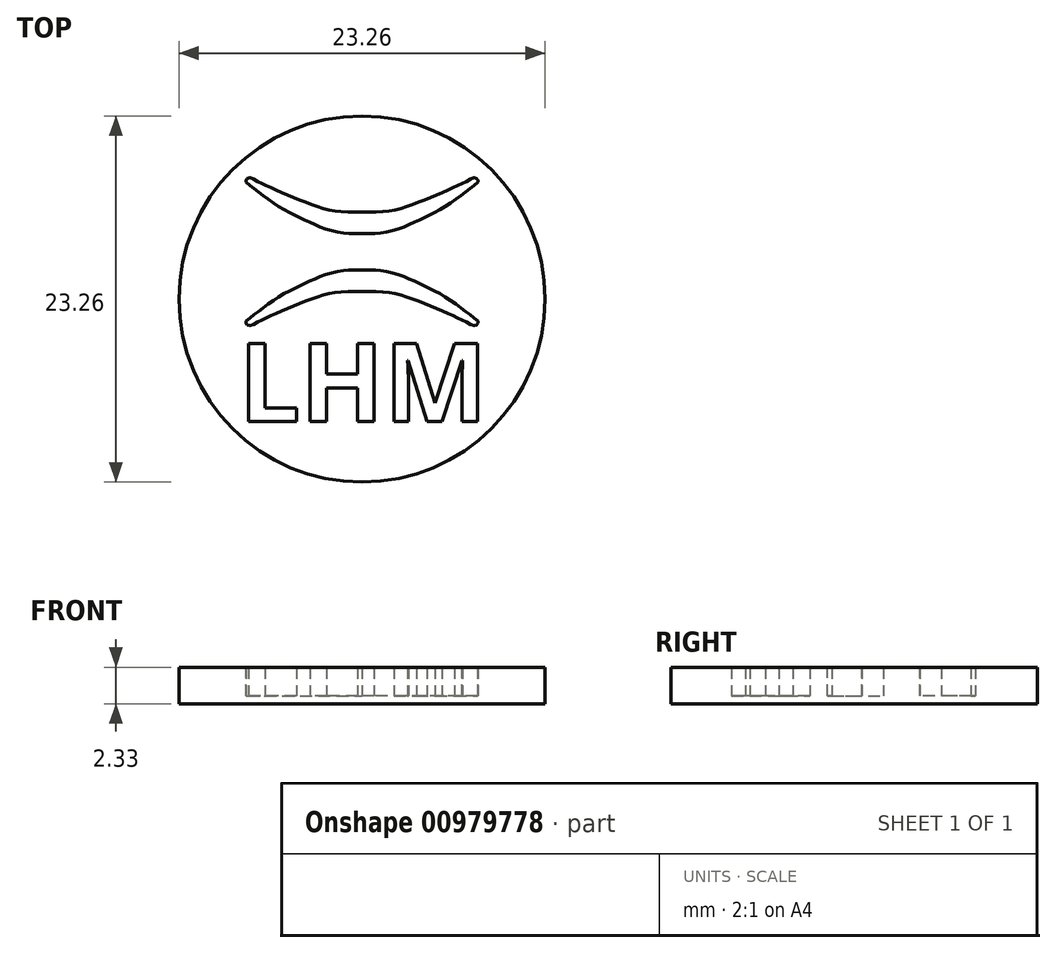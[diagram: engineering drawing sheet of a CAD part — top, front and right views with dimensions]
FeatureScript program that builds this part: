
annotation { "Feature Type Name" : "Feature", "Feature Type Description" : "" }
export const myFeature = defineFeature(function(context is Context, id is Id, definition is map)
    precondition{}
    {
        {
            var Q0;
            Q0=qCreatedBy(makeId("Top.planeOp"),FACE);
            var sketch = newSketch(context, id + "F0", { "sketchPlane" : qUnion([Q0])});
            skCircle(sketch, "E0", {"center": v(0, 0) * mm, "radius": 11.62 * mm});
            skFitSpline(sketch, "E1", {"points": [v(-7.37, 7.42) * mm, v(-6.39, 6.65) * mm, v(-4.92, 5.66) * mm, v(-3.64, 5.04) * mm, v(-2.33, 4.47) * mm, v(-0.84, 4.17) * mm, v(0, 4.17) * mm], "startDerivative": vector(5.75, -4.65) * mm, "endDerivative": vector(5.88, 0.29) * mm});
            skFitSpline(sketch, "E2", {"points": [v(-7.37, 7.42) * mm, v(-7.37, 7.54) * mm, v(-7.2, 7.7) * mm, v(-6.66, 7.5) * mm, v(-5.84, 7.1) * mm, v(-4.57, 6.55) * mm, v(-3.07, 5.96) * mm, v(-1.75, 5.6) * mm, v(0, 5.54) * mm], "startDerivative": vector(-0.42, 2.27) * mm, "endDerivative": vector(10.34, 0.08) * mm});
            skFitSpline(sketch, "E3.MirrorCS", {"points": [v(7.37, 7.42) * mm, v(7.37, 7.54) * mm, v(7.2, 7.7) * mm, v(6.66, 7.5) * mm, v(5.84, 7.1) * mm, v(4.57, 6.55) * mm, v(3.07, 5.96) * mm, v(1.75, 5.6) * mm, v(0, 5.54) * mm], "startDerivative": vector(0.42, 2.27) * mm, "endDerivative": vector(-10.34, 0.08) * mm});
            skFitSpline(sketch, "E4.MirrorCS", {"points": [v(7.37, 7.42) * mm, v(6.39, 6.65) * mm, v(4.92, 5.66) * mm, v(3.64, 5.04) * mm, v(2.33, 4.47) * mm, v(0.84, 4.17) * mm, v(0, 4.17) * mm], "startDerivative": vector(-5.75, -4.65) * mm, "endDerivative": vector(-5.88, 0.29) * mm});
            skFitSpline(sketch, "E5.MirrorCS", {"points": [v(-7.37, -1.4) * mm, v(-6.39, -0.63) * mm, v(-4.92, 0.36) * mm, v(-3.64, 0.98) * mm, v(-2.33, 1.55) * mm, v(-0.84, 1.85) * mm, v(0, 1.85) * mm], "startDerivative": vector(5.75, 4.65) * mm, "endDerivative": vector(5.88, -0.29) * mm});
            skFitSpline(sketch, "E6.MirrorCS", {"points": [v(7.37, -1.4) * mm, v(6.39, -0.63) * mm, v(4.92, 0.36) * mm, v(3.64, 0.98) * mm, v(2.33, 1.55) * mm, v(0.84, 1.85) * mm, v(0, 1.85) * mm], "startDerivative": vector(-5.75, 4.65) * mm, "endDerivative": vector(-5.88, -0.29) * mm});
            skFitSpline(sketch, "E7.MirrorCS", {"points": [v(7.37, -1.4) * mm, v(7.37, -1.51) * mm, v(7.2, -1.69) * mm, v(6.66, -1.48) * mm, v(5.84, -1.08) * mm, v(4.57, -0.53) * mm, v(3.07, 0.06) * mm, v(1.75, 0.42) * mm, v(0, 0.48) * mm], "startDerivative": vector(0.42, -2.27) * mm, "endDerivative": vector(-10.34, -0.08) * mm});
            skFitSpline(sketch, "E8.MirrorCS", {"points": [v(-7.37, -1.4) * mm, v(-7.37, -1.51) * mm, v(-7.2, -1.69) * mm, v(-6.66, -1.48) * mm, v(-5.84, -1.08) * mm, v(-4.57, -0.53) * mm, v(-3.07, 0.06) * mm, v(-1.75, 0.42) * mm, v(0, 0.48) * mm], "startDerivative": vector(-0.42, -2.27) * mm, "endDerivative": vector(10.34, -0.08) * mm});
            skText(sketch, "E9", { "text": "LHM", "fontName": "OpenSans-Bold.ttf"});
            const initialGuessF0  = {"E9": [-0.00784, -0.00778, 1, 0, 0.005]};
            skSetInitialGuess(sketch, initialGuessF0);
            skSolve(sketch);
        }
        {
            var Q0;
            Q0=makeQuery(id+"F0.imprint","IMPRINT",FACE,{"disambiguationData":[TD([[makeQuery(id+"F0.imprint","IMPRINT",EDGE,{"derivedFrom":sQuery(id+"F0.wireOp",EDGE,"E0")}),1.0]])]});
            extrude(context, id + "F1", {"entities" : qUnion([Q0]), "depth" : 2.33 * mm, "offsetDistance" : 25 * mm});
        }
        {
            var Q0;
            Q0=makeQuery(id+"F0.imprint","IMPRINT",FACE,{"disambiguationData":[TD([[makeQuery(id+"F0.imprint","IMPRINT",EDGE,{"derivedFrom":sQuery(id+"F0.wireOp",EDGE,"E5.MirrorCS")}),-1.0]])]});
            var Q1;
            Q1=makeQuery(id+"F0.imprint","IMPRINT",FACE,{"disambiguationData":[TD([[makeQuery(id+"F0.imprint","IMPRINT",EDGE,{"derivedFrom":sQuery(id+"F0.wireOp",EDGE,"E1")}),1.0]])]});
            extrude(context, id + "F2", {"entities" : qUnion([Q0, Q1]), "operationType" : NewBodyOperationType.ADD, "depth" : 0.5 * mm, "offsetDistance" : 25 * mm});
        }
        {
            var Q0;
            Q0=makeQuery(id+"F0.imprint","IMPRINT",FACE,{"disambiguationData":[TD([[makeQuery(id+"F0.imprint","IMPRINT",EDGE,{"derivedFrom":sQuery(id+"F0.wireOp",EDGE,"E9.sketch_text.stroke-0")}),-1.0]])]});
            var Q1;
            Q1=makeQuery(id+"F0.imprint","IMPRINT",FACE,{"disambiguationData":[TD([[makeQuery(id+"F0.imprint","IMPRINT",EDGE,{"derivedFrom":sQuery(id+"F0.wireOp",EDGE,"E9.sketch_text.stroke-18")}),-1.0]])]});
            var Q2;
            Q2=makeQuery(id+"F0.imprint","IMPRINT",FACE,{"disambiguationData":[TD([[makeQuery(id+"F0.imprint","IMPRINT",EDGE,{"derivedFrom":sQuery(id+"F0.wireOp",EDGE,"E9.sketch_text.stroke-6")}),-1.0]])]});
            extrude(context, id + "F3", {"entities" : qUnion([Q0, Q1, Q2]), "operationType" : NewBodyOperationType.ADD, "depth" : 0.5 * mm, "offsetDistance" : 25 * mm});
        }
    });
